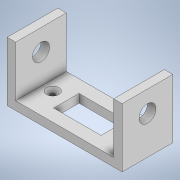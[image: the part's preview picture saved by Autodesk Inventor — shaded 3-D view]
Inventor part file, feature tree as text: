
AUTODESK INVENTOR PART (.ipt)
format: ipt  version: 2022 (Build 260153000, 153)  size: 148,992 bytes
history: native  units: mm
features: sketch x6, extrude x5
ambient origin geometry x8: Origin, YZ Plane, XZ Plane, XY Plane, X Axis, Y Axis, Z Axis, Center Point
bodies: Solid1 (feature_tree)
feature tree (11):
  extrude  "Extrusion1"  Depth=5.0mm
  extrude  "Extrusion2"  Depth=58.0mm
  extrude  "Extrusion3"  Depth=5.0mm
  extrude  "Extrusion4"  Depth=10.0mm
  extrude  "Extrusion5"  Depth=15.0mm
  sketch  "Sketch6"  dims[d11=0.0mm d12=0.0mm d13=28.0mm d14=15.0mm d15=15.0mm d16=29.0mm d17=0.0mm d18=0.0mm d19=7.25mm d20=6.0mm d21=7.25mm d22=9.0mm d23=2.1735mm d24=-7.853982mm d25=0.0mm d26=0.0mm]
  sketch  "Sketch1"  dims[d0=35.0mm d1=5.0mm]
  sketch  "Sketch2"  dims[d2=30.0mm d3=58.0mm]
  sketch  "Sketch3"  dims[d4=30.0mm d5=5.0mm]
  sketch  "Sketch4"  dims[d6=30.0mm d7=0.0mm d8=10.0mm]
  sketch  "Sketch5"  dims[d9=12.5mm d10=15.0mm]
